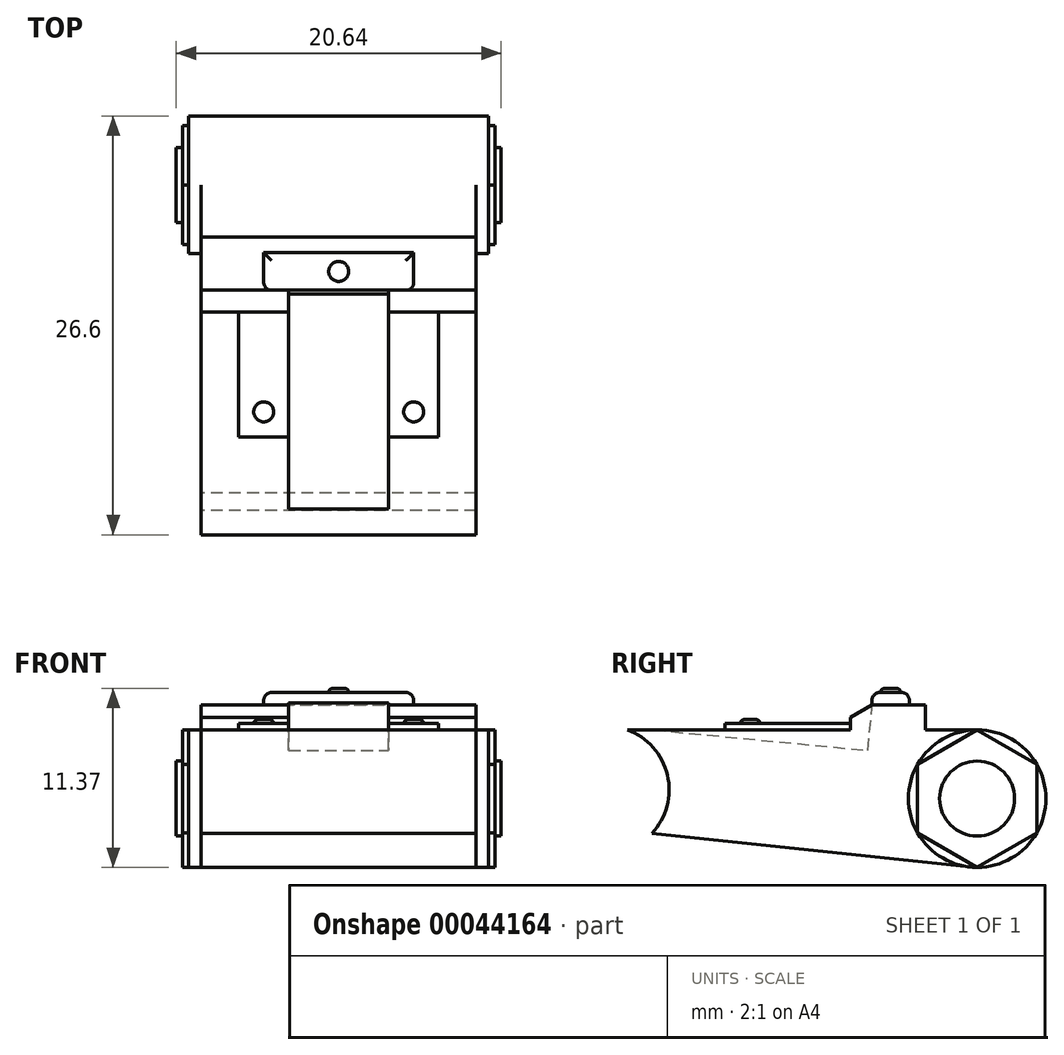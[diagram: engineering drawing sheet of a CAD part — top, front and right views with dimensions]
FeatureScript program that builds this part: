
annotation { "Feature Type Name" : "Feature", "Feature Type Description" : "" }
export const myFeature = defineFeature(function(context is Context, id is Id, definition is map)
    precondition{}
    {
        {
            var Q0;
            Q0=qCreatedBy(makeId("Right.planeOp"),FACE);
            var sketch = newSketch(context, id + "F0", { "sketchPlane" : qUnion([Q0])});
            skCircle(sketch, "E0", {"center": v(0, 0) * mm, "radius": 4.37 * mm});
            skLineSegment(sketch, "E1", {"start": v(0, 4.37) * mm, "end": v(-3.3, 4.37) * mm});
            skLineSegment(sketch, "E2", {"start": v(-0.46, -4.34) * mm, "end": v(-20.67, -2.22) * mm});
            skArc(sketch, "E3", {"start": v(-20.67, -2.22) * mm, "mid": v(-19.67, 1.5) * mm, "end": v(-22.23, 4.37) * mm});
            skLineSegment(sketch, "E4", {"start": v(-8.06, 4.37) * mm, "end": v(-8.06, 5.95) * mm});
            skLineSegment(sketch, "E5", {"start": v(-8.06, 5.95) * mm, "end": v(-3.3, 5.95) * mm});
            skLineSegment(sketch, "E6", {"start": v(-3.3, 5.95) * mm, "end": v(-3.3, 4.37) * mm});
            skLineSegment(sketch, "E7.trimOffspring", {"start": v(-8.06, 4.37) * mm, "end": v(-22.23, 4.37) * mm});
            skSolve(sketch);
        }
        {
            var Q0;
            {var subQ2=sQuery(id+"F0.wireOp",EDGE,"E1");Q0=makeQuery(id+"F0.imprint","IMPRINT",FACE,{"disambiguationData":[TD([[makeQuery(id+"F0.imprint","IMPRINT",EDGE,{"derivedFrom":subQ2}),1.0]])]});}
            extrude(context, id + "F1", {"entities" : qUnion([Q0]), "endBound" : BoundingType.SYMMETRIC, "depth" : 17.46 * mm});
        }
        {
            var Q0;
            Q0=qCreatedBy(makeId("Right.planeOp"),FACE);
            var sketch = newSketch(context, id + "F2", { "sketchPlane" : qUnion([Q0])});
            skCircle(sketch, "E8", {"center": v(0, 0) * mm, "radius": 4.37 * mm});
            skSolve(sketch);
        }
        {
            var Q0;
            Q0=qSketchRegion(id+"F2",true);
            extrude(context, id + "F3", {"entities" : qUnion([Q0]), "operationType" : NewBodyOperationType.ADD, "endBound" : BoundingType.SYMMETRIC, "depth" : 19.05 * mm});
        }
        {
            var Q0;
            Q0=makeQuery(id+"F3.opExtrude","CAP_FACE",FACE,{"disambiguationData":[OSD([sQuery(id+"F2.wireOp",EDGE,"E8")])],"isStart":false});
            var sketch = newSketch(context, id + "F4", { "sketchPlane" : qUnion([Q0])});
            skCircle(sketch, "E9.cCircle", {"center": v(0, 0) * mm, "radius": 4.37 * mm, "construction": true});
            skLineSegment(sketch, "E9.0", {"start": v(0, 4.37) * mm, "end": v(3.78, 2.18) * mm});
            skLineSegment(sketch, "E9.1", {"start": v(3.78, 2.18) * mm, "end": v(3.78, -2.18) * mm});
            skLineSegment(sketch, "E9.2", {"start": v(3.78, -2.18) * mm, "end": v(0, -4.37) * mm});
            skLineSegment(sketch, "E9.3", {"start": v(0, -4.37) * mm, "end": v(-3.78, -2.18) * mm});
            skLineSegment(sketch, "E9.4", {"start": v(-3.78, -2.18) * mm, "end": v(-3.78, 2.18) * mm});
            skLineSegment(sketch, "E9.5", {"start": v(-3.78, 2.18) * mm, "end": v(0, 4.37) * mm});
            skSolve(sketch);
        }
        {
            var Q0;
            Q0=qSketchRegion(id+"F4",true);
            extrude(context, id + "F5", {"entities" : qUnion([Q0]), "operationType" : NewBodyOperationType.ADD, "depth" : 0.4 * mm});
        }
        {
            var Q0;
            Q0=makeQuery(id+"F5.opExtrude","CAP_FACE",FACE,{"disambiguationData":[OSD([sQuery(id+"F4.wireOp",EDGE,"E9.0"),sQuery(id+"F4.wireOp",EDGE,"E9.1"),sQuery(id+"F4.wireOp",EDGE,"E9.2"),sQuery(id+"F4.wireOp",EDGE,"E9.3"),sQuery(id+"F4.wireOp",EDGE,"E9.4"),sQuery(id+"F4.wireOp",EDGE,"E9.5")])],"isStart":false});
            var sketch = newSketch(context, id + "F6", { "sketchPlane" : qUnion([Q0])});
            skCircle(sketch, "E10", {"center": v(0, 0) * mm, "radius": 2.38 * mm});
            skSolve(sketch);
        }
        {
            var Q0;
            Q0=makeQuery(id+"F6.imprint","IMPRINT",FACE,{"disambiguationData":[TD([[makeQuery(id+"F6.imprint","IMPRINT",EDGE,{"derivedFrom":sQuery(id+"F6.wireOp",EDGE,"E10")}),1.0]])]});
            extrude(context, id + "F7", {"entities" : qUnion([Q0]), "operationType" : NewBodyOperationType.ADD, "depth" : 0.4 * mm});
        }
        {
            var Q0;
            Q0=makeQuery(id+"F3.opExtrude","CAP_FACE",FACE,{"disambiguationData":[OSD([sQuery(id+"F2.wireOp",EDGE,"E8")])],"isStart":true});
            var sketch = newSketch(context, id + "F8", { "sketchPlane" : qUnion([Q0])});
            skCircle(sketch, "E11.cCircle", {"center": v(0, 0) * mm, "radius": 4.37 * mm, "construction": true});
            skLineSegment(sketch, "E11.0", {"start": v(0, 4.37) * mm, "end": v(3.78, 2.18) * mm});
            skLineSegment(sketch, "E11.1", {"start": v(3.78, 2.18) * mm, "end": v(3.78, -2.18) * mm});
            skLineSegment(sketch, "E11.2", {"start": v(3.78, -2.18) * mm, "end": v(0, -4.37) * mm});
            skLineSegment(sketch, "E11.3", {"start": v(0, -4.37) * mm, "end": v(-3.78, -2.18) * mm});
            skLineSegment(sketch, "E11.4", {"start": v(-3.78, -2.18) * mm, "end": v(-3.78, 2.18) * mm});
            skLineSegment(sketch, "E11.5", {"start": v(-3.78, 2.18) * mm, "end": v(0, 4.37) * mm});
            skSolve(sketch);
        }
        {
            var Q0;
            Q0=qSketchRegion(id+"F8",true);
            extrude(context, id + "F9", {"entities" : qUnion([Q0]), "operationType" : NewBodyOperationType.ADD, "depth" : 0.4 * mm});
        }
        {
            var Q0;
            Q0=makeQuery(id+"F9.opExtrude","CAP_FACE",FACE,{"disambiguationData":[OSD([sQuery(id+"F8.wireOp",EDGE,"E11.0"),sQuery(id+"F8.wireOp",EDGE,"E11.1"),sQuery(id+"F8.wireOp",EDGE,"E11.2"),sQuery(id+"F8.wireOp",EDGE,"E11.3"),sQuery(id+"F8.wireOp",EDGE,"E11.4"),sQuery(id+"F8.wireOp",EDGE,"E11.5")])],"isStart":false});
            var sketch = newSketch(context, id + "F10", { "sketchPlane" : qUnion([Q0])});
            skCircle(sketch, "E12", {"center": v(0, 0) * mm, "radius": 2.38 * mm});
            skSolve(sketch);
        }
        {
            var Q0;
            Q0=makeQuery(id+"F10.imprint","IMPRINT",FACE,{"disambiguationData":[TD([[makeQuery(id+"F10.imprint","IMPRINT",EDGE,{"derivedFrom":sQuery(id+"F10.wireOp",EDGE,"E12")}),1.0]])]});
            extrude(context, id + "F11", {"entities" : qUnion([Q0]), "operationType" : NewBodyOperationType.ADD, "depth" : 0.4 * mm});
        }
        {
            var Q0;
            {var subQ0=sQuery(id+"F0.wireOp",EDGE,"E4");var subQ1=sQuery(id+"F0.wireOp",EDGE,"E5");Q0=makeQuery(id+"FYXai5P5q28vsgm_1.boolean.opBoolean","SPLIT",EDGE,{"disambiguationData":[TD([makeQuery(id+"FYXai5P5q28vsgm_1.opExtrude","SWEPT_FACE",FACE,{"disambiguationData":[OSD([sQuery(id+"F1tNzmNj4fN5JQL_1.wireOp",EDGE,"af41d75d-76c8-4b64-93ca-d20af486b52f")])]})])],"derivedFrom":makeQuery(id+"F1.opExtrude","SWEPT_EDGE",EDGE,{"disambiguationData":[OSD([subQ0,subQ1])]})});}
            var Q1;
            {var subQ0=sQuery(id+"F0.wireOp",EDGE,"E4");var subQ1=sQuery(id+"F0.wireOp",EDGE,"E5");Q1=makeQuery(id+"FYXai5P5q28vsgm_1.boolean.opBoolean","SPLIT",EDGE,{"disambiguationData":[TD([makeQuery(id+"FYXai5P5q28vsgm_1.opExtrude","SWEPT_FACE",FACE,{"disambiguationData":[OSD([sQuery(id+"F1tNzmNj4fN5JQL_1.wireOp",EDGE,"c9f36269-9b65-402b-a7ed-104d228f7e5f")])]})])],"derivedFrom":makeQuery(id+"F1.opExtrude","SWEPT_EDGE",EDGE,{"disambiguationData":[OSD([subQ0,subQ1])]})});}
            chamfer(context, id + "F12", {"entities" : qUnion([Q0, Q1]), "chamferType" : ChamferType.OFFSET_ANGLE, "width" : 0.8 * mm, "oppositeDirection" : false, "angle" : 60 * degree, "tangentPropagation" : true});
        }
        {
            var Q0;
            Q0=makeQuery(id+"F1.opExtrude","SWEPT_FACE",FACE,{"disambiguationData":[OSD([sQuery(id+"F0.wireOp",EDGE,"E7.trimOffspring")])]});
            var sketch = newSketch(context, id + "F13", { "sketchPlane" : qUnion([Q0])});
            skLineSegment(sketch, "E13.bottom", {"start": v(-3.17, -8.06) * mm, "end": v(-6.35, -8.06) * mm});
            skLineSegment(sketch, "E13.top", {"start": v(-3.17, -16) * mm, "end": v(-6.35, -16) * mm});
            skLineSegment(sketch, "E13.left", {"start": v(-3.17, -8.06) * mm, "end": v(-3.17, -16) * mm});
            skLineSegment(sketch, "E13.right", {"start": v(-6.35, -8.06) * mm, "end": v(-6.35, -16) * mm});
            skPoint(sketch, "E14.oppositeSnap0", {"position": v(-4.76, -16) * mm});
            skLineSegment(sketch, "E14.bottom", {"start": v(3.17, -8.06) * mm, "end": v(6.35, -8.06) * mm});
            skLineSegment(sketch, "E14.top", {"start": v(3.18, -16) * mm, "end": v(6.35, -16) * mm});
            skLineSegment(sketch, "E14.left", {"start": v(3.17, -8.06) * mm, "end": v(3.17, -16) * mm});
            skLineSegment(sketch, "E14.right", {"start": v(6.35, -8.06) * mm, "end": v(6.35, -16) * mm});
            skSolve(sketch);
        }
        {
            var Q0;
            Q0=makeQuery(id+"F13.imprint","IMPRINT",FACE,{"disambiguationData":[TD([[makeQuery(id+"F13.imprint","IMPRINT",EDGE,{"derivedFrom":sQuery(id+"F13.wireOp",EDGE,"E13.bottom")}),1.0]])]});
            var Q1;
            Q1=makeQuery(id+"F13.imprint","IMPRINT",FACE,{"disambiguationData":[TD([[makeQuery(id+"F13.imprint","IMPRINT",EDGE,{"derivedFrom":sQuery(id+"F13.wireOp",EDGE,"E14.bottom")}),1.0]])]});
            extrude(context, id + "F14", {"entities" : qUnion([Q0, Q1]), "operationType" : NewBodyOperationType.ADD, "depth" : 0.4 * mm});
        }
        {
            var Q0;
            Q0=makeQuery(id+"F14.opExtrude","CAP_FACE",FACE,{"disambiguationData":[OSD([sQuery(id+"F13.wireOp",EDGE,"E13.bottom"),sQuery(id+"F13.wireOp",EDGE,"E13.top"),sQuery(id+"F13.wireOp",EDGE,"E13.left"),sQuery(id+"F13.wireOp",EDGE,"E13.right")])],"isStart":false});
            var sketch = newSketch(context, id + "F15", { "sketchPlane" : qUnion([Q0])});
            skLineSegment(sketch, "E15", {"start": v(-4.76, -16) * mm, "end": v(-4.76, -14.41) * mm});
            skCircle(sketch, "E16", {"center": v(-4.76, -14.41) * mm, "radius": 0.64 * mm});
            skSolve(sketch);
        }
        {
            var Q0;
            Q0=makeQuery(id+"F15.imprint","IMPRINT",FACE,{"disambiguationData":[TD([[makeQuery(id+"F15.imprint","IMPRINT",EDGE,{"derivedFrom":sQuery(id+"F15.wireOp",EDGE,"E16")}),1.0]])]});
            extrude(context, id + "F16", {"entities" : qUnion([Q0]), "operationType" : NewBodyOperationType.ADD, "depth" : 0.25 * mm});
        }
        {
            var Q0;
            Q0=makeQuery(id+"F14.opExtrude","CAP_FACE",FACE,{"disambiguationData":[OSD([sQuery(id+"F13.wireOp",EDGE,"E14.bottom"),sQuery(id+"F13.wireOp",EDGE,"E14.top"),sQuery(id+"F13.wireOp",EDGE,"E14.left"),sQuery(id+"F13.wireOp",EDGE,"E14.right")])],"isStart":false});
            var sketch = newSketch(context, id + "F17", { "sketchPlane" : qUnion([Q0])});
            skLineSegment(sketch, "E17", {"start": v(4.76, -16) * mm, "end": v(4.76, -14.41) * mm});
            skCircle(sketch, "E18", {"center": v(4.76, -14.41) * mm, "radius": 0.64 * mm});
            skSolve(sketch);
        }
        {
            var Q0;
            Q0=makeQuery(id+"F17.imprint","IMPRINT",FACE,{"disambiguationData":[TD([[makeQuery(id+"F17.imprint","IMPRINT",EDGE,{"derivedFrom":sQuery(id+"F17.wireOp",EDGE,"E18")}),1.0]])]});
            extrude(context, id + "F18", {"entities" : qUnion([Q0]), "operationType" : NewBodyOperationType.ADD, "depth" : 0.25 * mm});
        }
        {
            var Q0;
            Q0=makeQuery(id+"F1.opExtrude","SWEPT_FACE",FACE,{"disambiguationData":[OSD([sQuery(id+"F0.wireOp",EDGE,"E5")])]});
            var sketch = newSketch(context, id + "F19", { "sketchPlane" : qUnion([Q0])});
            skLineSegment(sketch, "E19.bottom", {"start": v(-4.76, -6.69) * mm, "end": v(4.76, -6.69) * mm});
            skLineSegment(sketch, "E19.top", {"start": v(-4.76, -4.3) * mm, "end": v(4.76, -4.3) * mm});
            skLineSegment(sketch, "E19.left", {"start": v(-4.76, -6.69) * mm, "end": v(-4.76, -4.3) * mm});
            skLineSegment(sketch, "E19.right", {"start": v(4.76, -6.69) * mm, "end": v(4.76, -4.3) * mm});
            skSolve(sketch);
        }
        {
            var Q0;
            Q0=makeQuery(id+"F19.imprint","IMPRINT",FACE,{"disambiguationData":[TD([[makeQuery(id+"F19.imprint","IMPRINT",EDGE,{"derivedFrom":sQuery(id+"F19.wireOp",EDGE,"E19.top")}),-1.0]])]});
            var Q1;
            {var subQ1=makeQuery(id+"FYXai5P5q28vsgm_1.boolean.opBoolean","COPY",EDGE,{"derivedFrom":makeQuery(id+"FYXai5P5q28vsgm_1.opExtrude","CAP_EDGE",EDGE,{"disambiguationData":[OSD([sQuery(id+"F1tNzmNj4fN5JQL_1.wireOp",EDGE,"af41d75d-76c8-4b64-93ca-d20af486b52f")])],"isStart":true})});Q1=makeQuery(id+"F19.imprint","IMPRINT",FACE,{"disambiguationData":[TD([[makeQuery(id+"F19.imprint","IMPRINT",EDGE,{"derivedFrom":subQ1}),-1.0]])]});}
            extrude(context, id + "F20", {"entities" : qUnion([Q0, Q1]), "operationType" : NewBodyOperationType.ADD, "depth" : 0.8 * mm});
        }
        {
            var Q0;
            Q0=makeQuery(id+"F16.opExtrude","CAP_EDGE",EDGE,{"disambiguationData":[OSD([sQuery(id+"F15.wireOp",EDGE,"E16")])],"isStart":false});
            var Q1;
            Q1=makeQuery(id+"F18.opExtrude","CAP_EDGE",EDGE,{"disambiguationData":[OSD([sQuery(id+"F17.wireOp",EDGE,"E18")])],"isStart":false});
            var Q2;
            Q2=makeQuery(id+"FcoPLUS2J54ZZGs_1.opExtrude","CAP_EDGE",EDGE,{"disambiguationData":[OSD([sQuery(id+"FEIiLctiWF2mMxl_1.wireOp",EDGE,"23d6f4f8-81ae-47a4-b10d-16c9256b85bb")])],"isStart":false});
            fillet(context, id + "F21", {"entities" : qUnion([Q0, Q1, Q2]), "radius" : 0.25 * mm, "tangentPropagation" : true, "allowEdgeOverflow" : false});
        }
        {
            var Q0;
            Q0=makeQuery(id+"F20.opExtrude","CAP_EDGE",EDGE,{"disambiguationData":[OSD([sQuery(id+"F19.wireOp",EDGE,"E19.left")])],"isStart":false});
            var Q1;
            Q1=makeQuery(id+"F20.opExtrude","CAP_EDGE",EDGE,{"disambiguationData":[OSD([sQuery(id+"F19.wireOp",EDGE,"E19.top")])],"isStart":false});
            var Q2;
            Q2=makeQuery(id+"F20.opExtrude","CAP_EDGE",EDGE,{"disambiguationData":[OSD([sQuery(id+"F19.wireOp",EDGE,"E19.right")])],"isStart":false});
            fillet(context, id + "F22", {"entities" : qUnion([Q0, Q1, Q2]), "radius" : 0.5 * mm, "tangentPropagation" : true, "allowEdgeOverflow" : false});
        }
        {
            var Q0;
            {var subQ0=sQuery(id+"F19.wireOp",EDGE,"E19.bottom");var subQ6=sQuery(id+"F19.wireOp",EDGE,"E19.left");Q0=makeQuery(id+"FcqncRxx0XAENAe_2.opBoolean","SPLIT",EDGE,{"disambiguationData":[TD([makeQuery(id+"F22.opFillet","BLEND_FACE",FACE,{"disambiguationData":[OSD([subQ6])]})])],"derivedFrom":makeQuery(id+"F20.opExtrude","CAP_EDGE",EDGE,{"disambiguationData":[OSD([subQ0])],"isStart":false})});}
            var Q1;
            {var subQ0=sQuery(id+"F19.wireOp",EDGE,"E19.bottom");var subQ1=sQuery(id+"F19.wireOp",EDGE,"E19.right");Q1=makeQuery(id+"FcqncRxx0XAENAe_2.opBoolean","SPLIT",EDGE,{"disambiguationData":[TD([makeQuery(id+"F22.opFillet","BLEND_FACE",FACE,{"disambiguationData":[OSD([subQ1])]})])],"derivedFrom":makeQuery(id+"F20.opExtrude","CAP_EDGE",EDGE,{"disambiguationData":[OSD([subQ0])],"isStart":false})});}
            fillet(context, id + "F23", {"entities" : qUnion([Q0, Q1]), "radius" : 0.5 * mm, "tangentPropagation" : true, "allowEdgeOverflow" : false});
        }
        {
            var Q0;
            Q0=qCreatedBy(makeId("Right.planeOp"),FACE);
            var sketch = newSketch(context, id + "F24", { "sketchPlane" : qUnion([Q0])});
            skLineSegment(sketch, "E20", {"start": v(-6.94, 3.06) * mm, "end": v(-6.65, 6.1) * mm});
            skLineSegment(sketch, "E21", {"start": v(-22.79, 4.58) * mm, "end": v(-6.94, 3.06) * mm});
            skLineSegment(sketch, "E22", {"start": v(-22.79, 4.58) * mm, "end": v(-6.65, 6.1) * mm});
            skSolve(sketch);
        }
        {
            var Q0;
            Q0 = qSketchRegion(id + "F24", true);
            extrude(context, id + "F25", {"entities" : qUnion([Q0]), "operationType" : NewBodyOperationType.REMOVE, "endBound" : BoundingType.SYMMETRIC, "oppositeDirection" : true, "depth" : 6.35 * mm});
        }
        {
            var Q0;
            Q0=makeQuery(id+"F20.opExtrude","CAP_FACE",FACE,{"disambiguationData":[OSD([sQuery(id+"F19.wireOp",EDGE,"E19.bottom"),sQuery(id+"F19.wireOp",EDGE,"E19.top"),sQuery(id+"F19.wireOp",EDGE,"E19.left"),sQuery(id+"F19.wireOp",EDGE,"E19.right")])],"isStart":false});
            var sketch = newSketch(context, id + "F26", { "sketchPlane" : qUnion([Q0])});
            skPoint(sketch, "E23.centerSnap0", {"position": v(0, -6.18) * mm});
            skLineSegment(sketch, "E24", {"start": v(0, -6.18) * mm, "end": v(0, -4.82) * mm});
            skCircle(sketch, "E25", {"center": v(0, -5.5) * mm, "radius": 0.64 * mm});
            skSolve(sketch);
        }
        {
            var Q0;
            Q0 = qSketchRegion(id + "F26", true);
            extrude(context, id + "F27", {"entities" : qUnion([Q0]), "operationType" : NewBodyOperationType.ADD, "depth" : 0.25 * mm});
        }
        {
            var Q0;
            Q0=makeQuery(id+"F27.opExtrude","CAP_EDGE",EDGE,{"disambiguationData":[OSD([sQuery(id+"F26.wireOp",EDGE,"E25")])],"isStart":false});
            fillet(context, id + "F28", {"entities" : qUnion([Q0]), "radius" : 0.25 * mm, "tangentPropagation" : true, "allowEdgeOverflow" : false});
        }
    });
